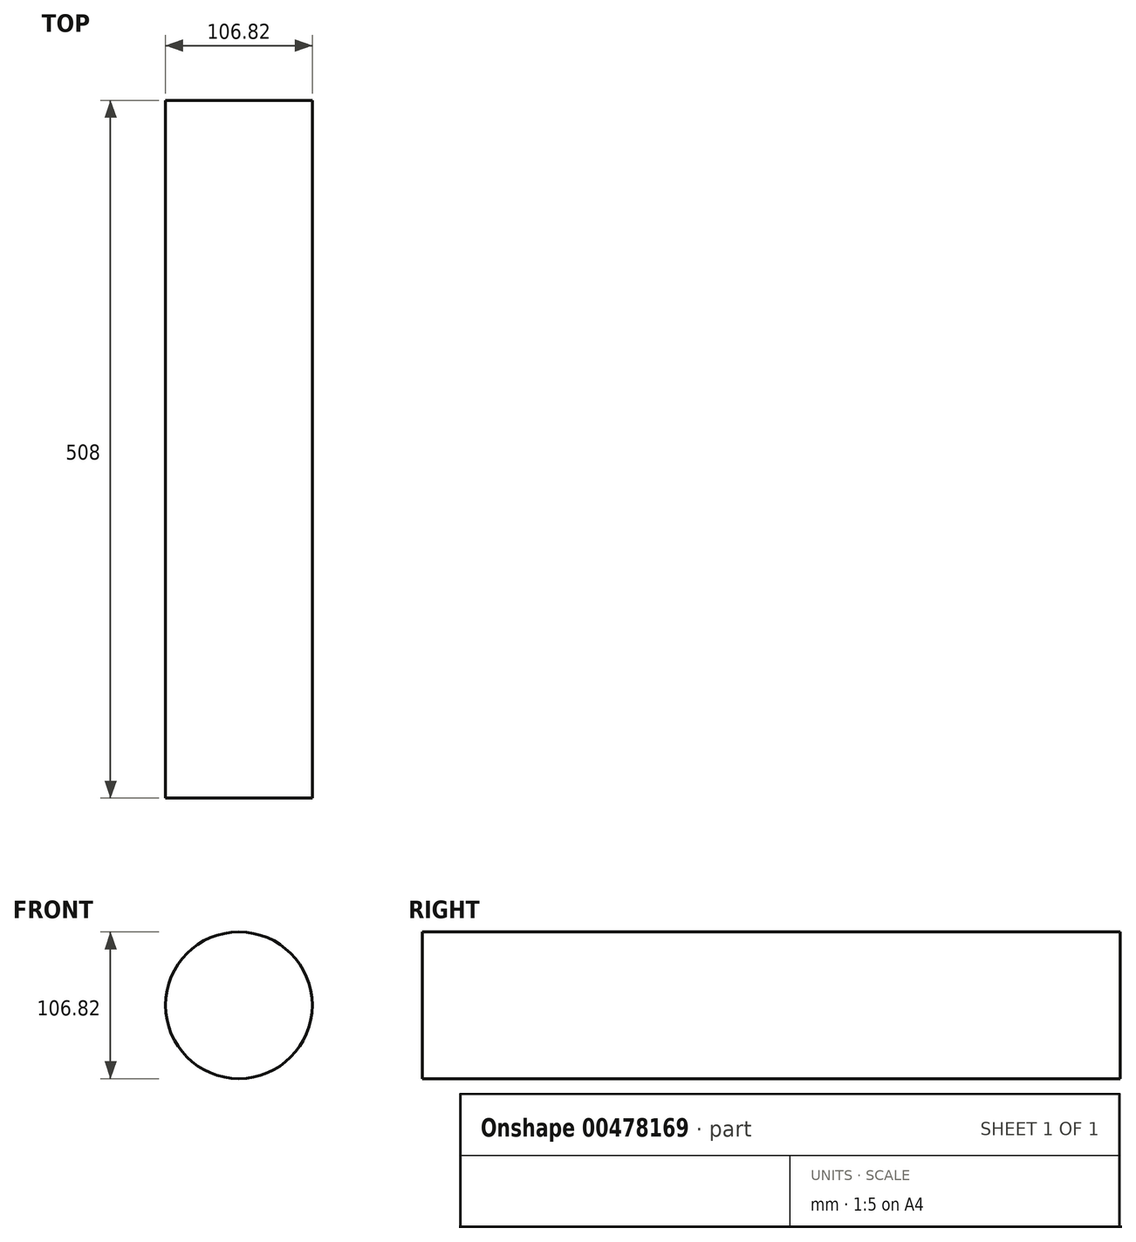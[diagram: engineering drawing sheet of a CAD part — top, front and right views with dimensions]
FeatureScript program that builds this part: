
annotation { "Feature Type Name" : "Feature", "Feature Type Description" : "" }
export const myFeature = defineFeature(function(context is Context, id is Id, definition is map)
    precondition{}
    {
        {
            var Q0;
            Q0=qCreatedBy(makeId("Front.planeOp"),FACE);
            var sketch = newSketch(context, id + "F0", { "sketchPlane" : qUnion([Q0])});
            skCircle(sketch, "E0", {"center": v(0, 0) * mm, "radius": 53.41 * mm});
            skSolve(sketch);
        }
        {
            var Q0;
            Q0 = qSketchRegion(id + "F0", true);
            extrude(context, id + "F1", {"entities" : qUnion([Q0]), "depth" : 508 * mm});
        }
    });
